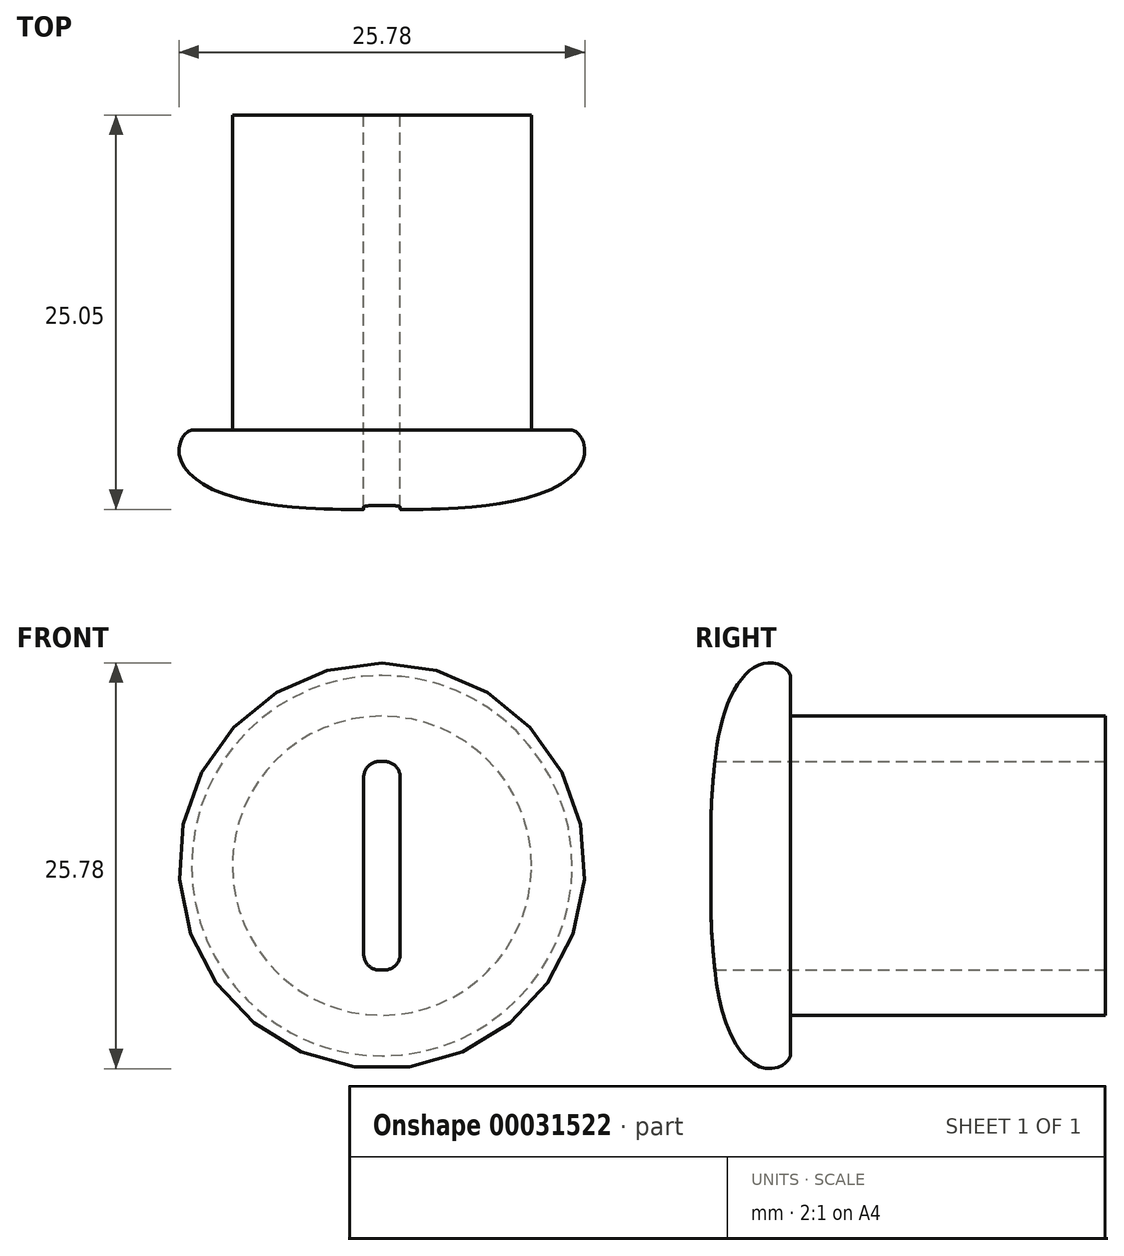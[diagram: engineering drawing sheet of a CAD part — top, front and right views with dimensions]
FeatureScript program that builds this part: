
annotation { "Feature Type Name" : "Feature", "Feature Type Description" : "" }
export const myFeature = defineFeature(function(context is Context, id is Id, definition is map)
    precondition{}
    {
        {
            var Q0;
            Q0=qCreatedBy(makeId("Right.planeOp"),FACE);
            var sketch = newSketch(context, id + "F0", { "sketchPlane" : qUnion([Q0])});
            skLineSegment(sketch, "E0", {"start": v(0, 0) * mm, "end": v(0, 9.5) * mm});
            skLineSegment(sketch, "E1", {"start": v(0, 9.5) * mm, "end": v(-20, 9.5) * mm});
            skLineSegment(sketch, "E2", {"start": v(-20, 9.5) * mm, "end": v(-20, 12.08) * mm});
            skLineSegment(sketch, "E3", {"start": v(0, 0) * mm, "end": v(-25, 0) * mm});
            skFitSpline(sketch, "E4", {"points": [v(-25, 0) * mm, v(-25, 4.17) * mm, v(-24, 10.26) * mm, v(-21.6, 12.87) * mm, v(-20, 12.08) * mm], "startDerivative": vector(-0.7, 28.93) * mm, "endDerivative": vector(3.45, -9.99) * mm});
            skSolve(sketch);
        }
        {
            var Q0;
            Q0=makeQuery(id+"F0.imprint","IMPRINT",FACE,{"disambiguationData":[TD([[makeQuery(id+"F0.imprint","IMPRINT",EDGE,{"derivedFrom":sQuery(id+"F0.wireOp",EDGE,"E0")}),1.0]])]});
            var Q1;
            Q1=sQuery(id+"F0.wireOp",EDGE,"E3");
            revolve(context, id + "F1", {"entities" : qUnion([Q0]), "axis" : qUnion([Q1]), "revolveType" : RevolveType.FULL});
        }
        {
            var Q0;
            Q0=makeQuery(id+"F1.opRevolve","SWEPT_FACE",FACE,{"disambiguationData":[OSD([sQuery(id+"F0.wireOp",EDGE,"E0")])]});
            var sketch = newSketch(context, id + "F2", { "sketchPlane" : qUnion([Q0])});
            skLineSegment(sketch, "E5.rect.bottom", {"start": v(0.16, 6.62) * mm, "end": v(-0.16, 6.62) * mm});
            skLineSegment(sketch, "E5.rect.top", {"start": v(0.16, -6.62) * mm, "end": v(-0.16, -6.62) * mm});
            skLineSegment(sketch, "E5.rect.left", {"start": v(1.16, 5.62) * mm, "end": v(1.16, -5.62) * mm});
            skLineSegment(sketch, "E5.rect.right", {"start": v(-1.16, 5.62) * mm, "end": v(-1.16, -5.62) * mm});
            skPoint(sketch, "E5.rect.middle", {"position": v(0, 0) * mm});
            skPoint(sketch, "E6.visualSharp", {"position": v(-1.16, 6.62) * mm});
            skArc(sketch, "E6.filletArc", {"start": v(-0.16, 6.62) * mm, "mid": v(-0.86, 6.33) * mm, "end": v(-1.16, 5.62) * mm});
            skPoint(sketch, "E7.visualSharp", {"position": v(1.16, 6.62) * mm});
            skArc(sketch, "E7.filletArc", {"start": v(1.16, 5.62) * mm, "mid": v(0.86, 6.33) * mm, "end": v(0.16, 6.62) * mm});
            skPoint(sketch, "E8.visualSharp", {"position": v(-1.16, -6.62) * mm});
            skArc(sketch, "E8.filletArc", {"start": v(-1.16, -5.62) * mm, "mid": v(-0.86, -6.33) * mm, "end": v(-0.16, -6.62) * mm});
            skPoint(sketch, "E9.visualSharp", {"position": v(1.16, -6.62) * mm});
            skArc(sketch, "E9.filletArc", {"start": v(0.16, -6.62) * mm, "mid": v(0.86, -6.33) * mm, "end": v(1.16, -5.62) * mm});
            skSolve(sketch);
        }
        {
            var Q0;
            Q0=makeQuery(id+"F2.imprint","IMPRINT",FACE,{"disambiguationData":[TD([[makeQuery(id+"F2.imprint","IMPRINT",EDGE,{"derivedFrom":sQuery(id+"F2.wireOp",EDGE,"E5.rect.bottom")}),1.0]])]});
            extrude(context, id + "F3", {"entities" : qUnion([Q0]), "operationType" : NewBodyOperationType.REMOVE, "endBound" : BoundingType.THROUGH_ALL, "oppositeDirection" : true, "depth" : 25 * mm});
        }
    });
